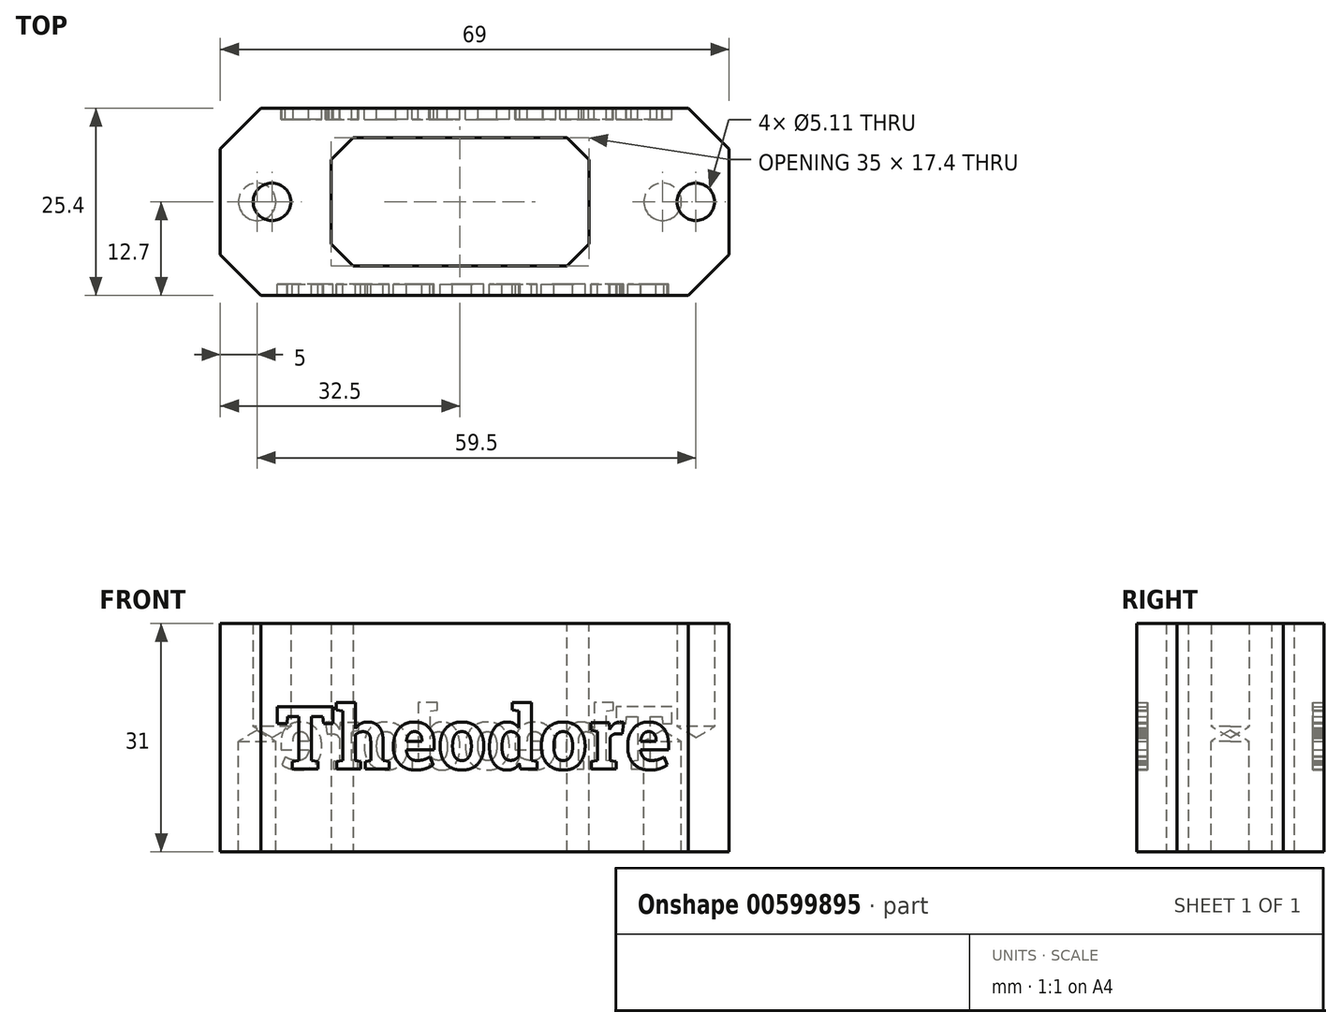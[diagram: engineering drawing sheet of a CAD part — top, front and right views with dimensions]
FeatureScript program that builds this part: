
annotation { "Feature Type Name" : "Feature", "Feature Type Description" : "" }
export const myFeature = defineFeature(function(context is Context, id is Id, definition is map)
    precondition{}
    {
        {
            var Q0;
            Q0=qCreatedBy(makeId("Top.planeOp"),FACE);
            var sketch = newSketch(context, id + "F0", { "sketchPlane" : qUnion([Q0])});
            skLineSegment(sketch, "E0.bottom", {"start": v(-69, 25.4) * mm, "end": v(0, 25.4) * mm});
            skLineSegment(sketch, "E0.top", {"start": v(-69, 0) * mm, "end": v(0, 0) * mm});
            skLineSegment(sketch, "E0.left", {"start": v(-69, 25.4) * mm, "end": v(-69, 0) * mm});
            skLineSegment(sketch, "E0.right", {"start": v(0, 25.4) * mm, "end": v(0, 0) * mm});
            skPoint(sketch, "E1", {"position": v(-64, 12.7) * mm});
            skPoint(sketch, "E2", {"position": v(-9, 12.7) * mm});
            skPoint(sketch, "E3", {"position": v(0, 12.7) * mm});
            skLineSegment(sketch, "E4.bottom", {"start": v(-54, 21.4) * mm, "end": v(-19, 21.4) * mm});
            skLineSegment(sketch, "E4.top", {"start": v(-54, 4) * mm, "end": v(-19, 4) * mm});
            skLineSegment(sketch, "E4.left", {"start": v(-54, 21.4) * mm, "end": v(-54, 4) * mm});
            skLineSegment(sketch, "E4.right", {"start": v(-19, 21.4) * mm, "end": v(-19, 4) * mm});
            skSolve(sketch);
        }
        {
            var Q0;
            Q0 = qSketchRegion(id + "F0", true);
            extrude(context, id + "F1", {"entities" : qUnion([Q0]), "depth" : 31 * mm, "offsetDistance" : 25 * mm});
        }
        {
            var Q0;
            Q0=sQuery(id+"F0.wireOp",VERTEX,"E1");
            var Q1;
            Q1=sQuery(id+"F0.wireOp",VERTEX,"E2");
            var Q2;
            Q2=makeQuery(id+"F1.opExtrude","SWEPT_BODY",BODY,{"disambiguationData":[OSD([sQuery(id+"F0.wireOp",EDGE,"E0.bottom"),sQuery(id+"F0.wireOp",EDGE,"E0.top"),sQuery(id+"F0.wireOp",EDGE,"E0.left"),sQuery(id+"F0.wireOp",EDGE,"E0.right")])]});
            hole(context, id + "F2", {"style" : HoleStyle.SIMPLE, "endStyle" : HoleEndStyle.BLIND, "oppositeDirection" : true, "standardTappedOrClearance" : lookupTablePath({ "standard" : "ANSI", "fit" : "Normal (ASME)", "size" : "#10", "type" : "Clearance" }), "standardBlindInLast" : lookupTablePath({ "fit" : "Free", "standard" : "ANSI", "size" : "#10", "type" : "Clearance" }), "holeDiameter" : 5.1 * mm, "majorDiameter" : 5 * mm, "holeDepth" : 15 * mm, "tappedDepth" : 12 * mm, "tapClearance" : 3, "locations" : qUnion([Q0, Q1]), "scope" : qUnion([Q2]), "startStyle" : HoleStartStyle.SKETCH});
        }
        {
            var Q0;
            Q0=makeQuery(id+"F1.opExtrude","CAP_FACE",FACE,{"disambiguationData":[OSD([sQuery(id+"F0.wireOp",EDGE,"E0.bottom"),sQuery(id+"F0.wireOp",EDGE,"E0.top"),sQuery(id+"F0.wireOp",EDGE,"E0.left"),sQuery(id+"F0.wireOp",EDGE,"E0.right")])],"isStart":false});
            var sketch = newSketch(context, id + "F3", { "sketchPlane" : qUnion([Q0])});
            skPoint(sketch, "E5", {"position": v(-62, 12.7) * mm});
            skPoint(sketch, "E6", {"position": v(-4.5, 12.7) * mm});
            skPoint(sketch, "E7", {"position": v(0, 12.7) * mm});
            skSolve(sketch);
        }
        {
            var Q0;
            Q0=sQuery(id+"F3.wireOp",VERTEX,"E5");
            var Q1;
            Q1=sQuery(id+"F3.wireOp",VERTEX,"E6");
            var Q2;
            Q2=makeQuery(id+"F1.opExtrude","SWEPT_BODY",BODY,{"disambiguationData":[OSD([sQuery(id+"F0.wireOp",EDGE,"E0.bottom"),sQuery(id+"F0.wireOp",EDGE,"E0.top"),sQuery(id+"F0.wireOp",EDGE,"E0.left"),sQuery(id+"F0.wireOp",EDGE,"E0.right")])]});
            hole(context, id + "F4", {"style" : HoleStyle.SIMPLE, "endStyle" : HoleEndStyle.BLIND, "standardTappedOrClearance" : lookupTablePath({ "standard" : "ANSI", "fit" : "Normal (ASME)", "size" : "#10", "type" : "Clearance" }), "standardBlindInLast" : lookupTablePath({ "fit" : "Free", "standard" : "ANSI", "size" : "#10", "type" : "Clearance" }), "holeDiameter" : 5.1 * mm, "majorDiameter" : 5 * mm, "holeDepth" : 14 * mm, "tappedDepth" : 12 * mm, "tapClearance" : 3, "locations" : qUnion([Q0, Q1]), "scope" : qUnion([Q2]), "startStyle" : HoleStartStyle.SKETCH});
        }
        {
            var Q0;
            Q0=makeQuery(id+"F1.opExtrude","SWEPT_EDGE",EDGE,{"disambiguationData":[OSD([sQuery(id+"F0.wireOp",EDGE,"E0.top"),sQuery(id+"F0.wireOp",EDGE,"E0.left")])]});
            var Q1;
            Q1=makeQuery(id+"F1.opExtrude","SWEPT_EDGE",EDGE,{"disambiguationData":[OSD([sQuery(id+"F0.wireOp",EDGE,"E0.top"),sQuery(id+"F0.wireOp",EDGE,"E0.right")])]});
            var Q2;
            Q2=makeQuery(id+"F1.opExtrude","SWEPT_EDGE",EDGE,{"disambiguationData":[OSD([sQuery(id+"F0.wireOp",EDGE,"E0.bottom"),sQuery(id+"F0.wireOp",EDGE,"E0.left")])]});
            var Q3;
            Q3=makeQuery(id+"F1.opExtrude","SWEPT_EDGE",EDGE,{"disambiguationData":[OSD([sQuery(id+"F0.wireOp",EDGE,"E0.bottom"),sQuery(id+"F0.wireOp",EDGE,"E0.right")])]});
            chamfer(context, id + "F5", {"entities" : qUnion([Q0, Q1, Q2, Q3]), "width" : 5.5 * mm, "tangentPropagation" : true});
        }
        {
            var Q0;
            Q0=makeQuery(id+"F1.opExtrude","SWEPT_FACE",FACE,{"disambiguationData":[OSD([sQuery(id+"F0.wireOp",EDGE,"E0.bottom")])]});
            var sketch = newSketch(context, id + "F6", { "sketchPlane" : qUnion([Q0])});
            skText(sketch, "E8", { "text": "Theodore", "fontName": "RobotoSlab-Bold.ttf"});
            skPoint(sketch, "E9", {"position": v(5.5, 15.5) * mm});
            skPoint(sketch, "E10", {"position": v(7.5, 15.5) * mm});
            skPoint(sketch, "E11", {"position": v(34.5, 0) * mm});
            const initialGuessF6  = {"E8": [0.0075, 0.01121, 1, 0, 0.00858]};
            skSetInitialGuess(sketch, initialGuessF6);
            skSolve(sketch);
        }
        {
            var Q0;
            Q0=makeQuery(id+"F1.opExtrude","SWEPT_FACE",FACE,{"disambiguationData":[OSD([sQuery(id+"F0.wireOp",EDGE,"E0.top")])]});
            var sketch = newSketch(context, id + "F7", { "sketchPlane" : qUnion([Q0])});
            skText(sketch, "E12", { "text": "Theodore", "fontName": "RobotoSlab-Bold.ttf"});
            const initialGuessF7  = {"E12": [-0.0615, 0.01121, 1, 0, 0.00858]};
            skSetInitialGuess(sketch, initialGuessF7);
            skSolve(sketch);
        }
        {
            var Q0;
            Q0 = qSketchRegion(id + "F6", true);
            var Q1;
            Q1 = qSketchRegion(id + "F7", true);
            extrude(context, id + "F8", {"entities" : qUnion([Q0, Q1]), "operationType" : NewBodyOperationType.REMOVE, "oppositeDirection" : true, "depth" : 1.5 * mm, "offsetDistance" : 25 * mm, "hasSecondDirection" : true, "secondDirectionOppositeDirection" : false, "secondDirectionDepth" : 1.5 * mm});
        }
        {
            var Q0;
            Q0=makeQuery(id+"F1.opExtrude","SWEPT_EDGE",EDGE,{"disambiguationData":[OSD([sQuery(id+"F0.wireOp",EDGE,"E4.bottom"),sQuery(id+"F0.wireOp",EDGE,"E4.left")])]});
            var Q1;
            Q1=makeQuery(id+"F1.opExtrude","SWEPT_EDGE",EDGE,{"disambiguationData":[OSD([sQuery(id+"F0.wireOp",EDGE,"E4.bottom"),sQuery(id+"F0.wireOp",EDGE,"E4.right")])]});
            var Q2;
            Q2=makeQuery(id+"F1.opExtrude","SWEPT_EDGE",EDGE,{"disambiguationData":[OSD([sQuery(id+"F0.wireOp",EDGE,"E4.top"),sQuery(id+"F0.wireOp",EDGE,"E4.right")])]});
            var Q3;
            Q3=makeQuery(id+"F1.opExtrude","SWEPT_EDGE",EDGE,{"disambiguationData":[OSD([sQuery(id+"F0.wireOp",EDGE,"E4.top"),sQuery(id+"F0.wireOp",EDGE,"E4.left")])]});
            chamfer(context, id + "F9", {"entities" : qUnion([Q0, Q1, Q2, Q3]), "width" : 3 * mm, "tangentPropagation" : true});
        }
    });
